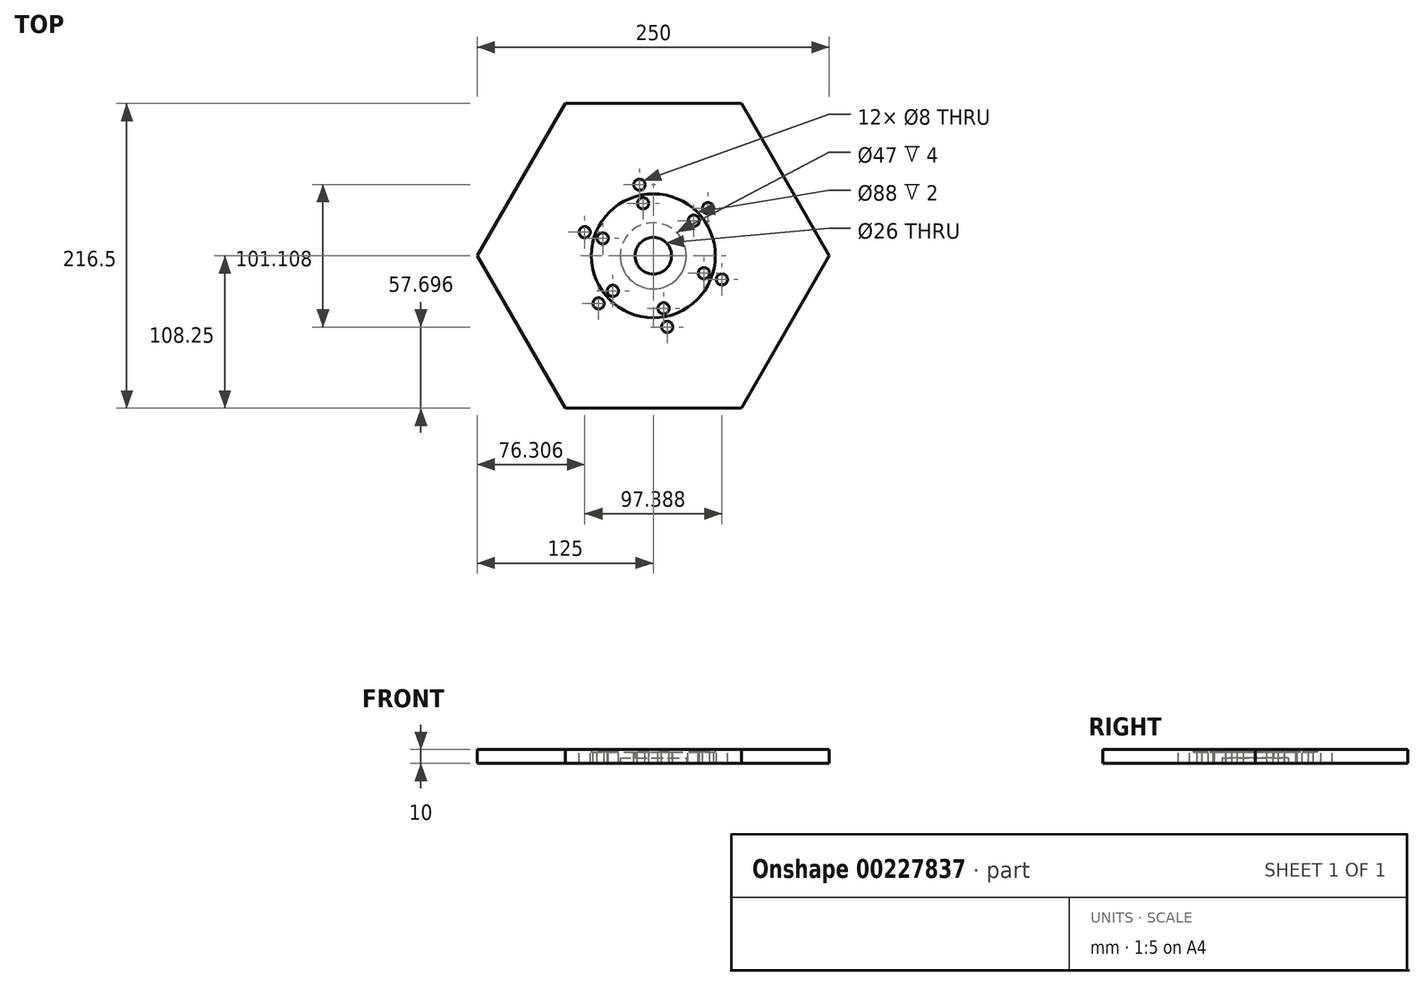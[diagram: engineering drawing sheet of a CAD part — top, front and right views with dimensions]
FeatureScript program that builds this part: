
annotation { "Feature Type Name" : "Feature", "Feature Type Description" : "" }
export const myFeature = defineFeature(function(context is Context, id is Id, definition is map)
    precondition{}
    {
        {
            var Q0;
            Q0=qCreatedBy(makeId("Top.planeOp"),FACE);
            var sketch = newSketch(context, id + "F0", { "sketchPlane" : qUnion([Q0])});
            skCircle(sketch, "E0.cCircle", {"center": v(0, 0) * mm, "radius": 125 * mm, "construction": true});
            skLineSegment(sketch, "E0.0", {"start": v(125, 0) * mm, "end": v(62.5, -108.25) * mm});
            skLineSegment(sketch, "E0.1", {"start": v(62.5, -108.25) * mm, "end": v(-62.5, -108.25) * mm});
            skLineSegment(sketch, "E0.2", {"start": v(-62.5, -108.25) * mm, "end": v(-125, 0) * mm});
            skLineSegment(sketch, "E0.3", {"start": v(-125, 0) * mm, "end": v(-62.5, 108.25) * mm});
            skLineSegment(sketch, "E0.4", {"start": v(-62.5, 108.25) * mm, "end": v(62.5, 108.25) * mm});
            skLineSegment(sketch, "E0.5", {"start": v(62.5, 108.25) * mm, "end": v(125, 0) * mm});
            skSolve(sketch);
        }
        {
            var Q0;
            Q0=makeQuery(id+"F0.imprint","IMPRINT",FACE,{"disambiguationData":[TD([[makeQuery(id+"F0.imprint","IMPRINT",EDGE,{"derivedFrom":sQuery(id+"F0.wireOp",EDGE,"E0.0")}),-1.0]])]});
            extrude(context, id + "F1", {"entities" : qUnion([Q0]), "depth" : 10 * mm});
        }
        {
            var Q0;
            Q0=qCreatedBy(makeId("Front.planeOp"),FACE);
            var sketch = newSketch(context, id + "F2", { "sketchPlane" : qUnion([Q0])});
            skLineSegment(sketch, "E1", {"start": v(0, 18) * mm, "end": v(0, -22.98) * mm, "construction": true});
            skLineSegment(sketch, "E2", {"start": v(-23.5, 0) * mm, "end": v(8.7, 0) * mm, "construction": true});
            skLineSegment(sketch, "E3", {"start": v(-23.5, -10) * mm, "end": v(0, -10) * mm});
            skLineSegment(sketch, "E4", {"start": v(-44, 18) * mm, "end": v(0, 18) * mm});
            skLineSegment(sketch, "E5", {"start": v(-23.5, 4) * mm, "end": v(-23.5, -10) * mm});
            skLineSegment(sketch, "E6", {"start": v(-23.5, 4) * mm, "end": v(-13, 4) * mm});
            skPoint(sketch, "E7.orphan", {"position": v(-23.5, 0) * mm});
            skLineSegment(sketch, "E8", {"start": v(0, 18) * mm, "end": v(0, -10) * mm});
            skLineSegment(sketch, "E9", {"start": v(-44, 8) * mm, "end": v(-13, 8) * mm});
            skLineSegment(sketch, "E10", {"start": v(-44, 18) * mm, "end": v(-44, 8) * mm});
            skLineSegment(sketch, "E11.trimOffspring", {"start": v(-13, 8) * mm, "end": v(-13, 4) * mm});
            skSolve(sketch);
        }
        {
            var Q0;
            Q0 = qSketchRegion(id + "F2", true);
            var Q1;
            Q1=sQuery(id+"F2.wireOp",EDGE,"E1");
            revolve(context, id + "F3", {"operationType" : NewBodyOperationType.REMOVE, "entities" : qUnion([Q0]), "axis" : qUnion([Q1]), "revolveType" : RevolveType.FULL, "oppositeDirection" : true});
        }
        {
            var Q0;
            Q0=makeQuery(id+"F1.opExtrude","CAP_FACE",FACE,{"disambiguationData":[OSD([sQuery(id+"F0.wireOp",EDGE,"E0.0"),sQuery(id+"F0.wireOp",EDGE,"E0.1"),sQuery(id+"F0.wireOp",EDGE,"E0.2"),sQuery(id+"F0.wireOp",EDGE,"E0.3"),sQuery(id+"F0.wireOp",EDGE,"E0.4"),sQuery(id+"F0.wireOp",EDGE,"E0.5")])],"isStart":false});
            var sketch = newSketch(context, id + "F4", { "sketchPlane" : qUnion([Q0])});
            skLineSegment(sketch, "E12", {"start": v(0.45, -2.3) * mm, "end": v(-8.01, 41.22) * mm, "construction": true});
            skPoint(sketch, "E13", {"position": v(0, 0) * mm});
            skLineSegment(sketch, "E14", {"start": v(2.66, 0.52) * mm, "end": v(-11.37, -2.2) * mm, "construction": true});
            skLineSegment(sketch, "E15", {"start": v(0, 0) * mm, "end": v(46.78, 40.67) * mm, "construction": true});
            skCircle(sketch, "E16", {"center": v(0, 0) * mm, "radius": 21.5 * mm, "construction": true});
            skLineSegment(sketch, "E17.1.1", {"start": v(0, 0) * mm, "end": v(58.6, -20.18) * mm, "construction": true});
            skLineSegment(sketch, "E17.2.1", {"start": v(0, 0) * mm, "end": v(11.83, -60.85) * mm, "construction": true});
            skLineSegment(sketch, "E17.3.1", {"start": v(0, 0) * mm, "end": v(-46.78, -40.67) * mm, "construction": true});
            skLineSegment(sketch, "E17.4.1", {"start": v(0, 0) * mm, "end": v(-58.6, 20.18) * mm, "construction": true});
            skLineSegment(sketch, "E17.5.1", {"start": v(0, 0) * mm, "end": v(-11.83, 60.85) * mm, "construction": true});
            skLineSegment(sketch, "E17.anchor2", {"start": v(0, 0) * mm, "end": v(-11.83, 60.85) * mm, "construction": true});
            skPoint(sketch, "E18", {"position": v(-16.23, -14.1) * mm});
            skCircle(sketch, "E19", {"center": v(0, 0) * mm, "radius": 38 * mm, "construction": true});
            skCircle(sketch, "E20", {"center": v(0, 0) * mm, "radius": 51.5 * mm, "construction": true});
            skPoint(sketch, "E21", {"position": v(-9.83, 50.55) * mm});
            skPoint(sketch, "E22", {"position": v(38.87, 33.79) * mm});
            skPoint(sketch, "E23", {"position": v(48.7, -16.77) * mm});
            skPoint(sketch, "E24", {"position": v(9.83, -50.55) * mm});
            skPoint(sketch, "E25", {"position": v(-38.87, -33.79) * mm});
            skPoint(sketch, "E26", {"position": v(-48.7, 16.77) * mm});
            skPoint(sketch, "E27", {"position": v(-7.25, 37.3) * mm});
            skPoint(sketch, "E28", {"position": v(28.68, 24.93) * mm});
            skPoint(sketch, "E29", {"position": v(35.93, -12.37) * mm});
            skPoint(sketch, "E30", {"position": v(7.25, -37.3) * mm});
            skPoint(sketch, "E31", {"position": v(-28.68, -24.93) * mm});
            skPoint(sketch, "E32", {"position": v(-35.93, 12.37) * mm});
            skPoint(sketch, "E33", {"position": v(-38.87, 63.66) * mm});
            skSolve(sketch);
        }
        {
            var Q0;
            Q0=sQuery(id+"F4.wireOp",VERTEX,"E21");
            var Q1;
            Q1=sQuery(id+"F4.wireOp",VERTEX,"E22");
            var Q2;
            Q2=sQuery(id+"F4.wireOp",VERTEX,"E23");
            var Q3;
            Q3=sQuery(id+"F4.wireOp",VERTEX,"E24");
            var Q4;
            Q4=sQuery(id+"F4.wireOp",VERTEX,"E25");
            var Q5;
            Q5=sQuery(id+"F4.wireOp",VERTEX,"E26");
            var Q6;
            Q6=makeQuery(id+"F1.opExtrude","SWEPT_BODY",BODY,{"disambiguationData":[OSD([sQuery(id+"F0.wireOp",EDGE,"E0.0"),sQuery(id+"F0.wireOp",EDGE,"E0.1"),sQuery(id+"F0.wireOp",EDGE,"E0.2"),sQuery(id+"F0.wireOp",EDGE,"E0.3"),sQuery(id+"F0.wireOp",EDGE,"E0.4"),sQuery(id+"F0.wireOp",EDGE,"E0.5")])]});
            hole(context, id + "F5", {"style" : HoleStyle.SIMPLE, "endStyle" : HoleEndStyle.BLIND, "holeDiameter" : 8 * mm, "holeDepth" : 15 * mm, "locations" : qUnion([Q0, Q1, Q2, Q3, Q4, Q5]), "scope" : qUnion([Q6])});
        }
        {
            var Q0;
            Q0=sQuery(id+"F4.wireOp",VERTEX,"E27");
            var Q1;
            Q1=sQuery(id+"F4.wireOp",VERTEX,"E28");
            var Q2;
            Q2=sQuery(id+"F4.wireOp",VERTEX,"E29");
            var Q3;
            Q3=sQuery(id+"F4.wireOp",VERTEX,"E30");
            var Q4;
            Q4=sQuery(id+"F4.wireOp",VERTEX,"E31");
            var Q5;
            Q5=sQuery(id+"F4.wireOp",VERTEX,"E32");
            var Q6;
            Q6=makeQuery(id+"F1.opExtrude","SWEPT_BODY",BODY,{"disambiguationData":[OSD([sQuery(id+"F0.wireOp",EDGE,"E0.0"),sQuery(id+"F0.wireOp",EDGE,"E0.1"),sQuery(id+"F0.wireOp",EDGE,"E0.2"),sQuery(id+"F0.wireOp",EDGE,"E0.3"),sQuery(id+"F0.wireOp",EDGE,"E0.4"),sQuery(id+"F0.wireOp",EDGE,"E0.5")])]});
            hole(context, id + "F6", {"style" : HoleStyle.SIMPLE, "endStyle" : HoleEndStyle.BLIND, "holeDiameter" : 8 * mm, "holeDepth" : 15 * mm, "locations" : qUnion([Q0, Q1, Q2, Q3, Q4, Q5]), "scope" : qUnion([Q6])});
        }
    });
